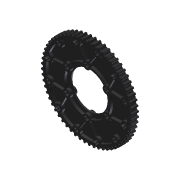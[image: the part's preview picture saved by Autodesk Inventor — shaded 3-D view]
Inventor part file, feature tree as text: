
AUTODESK INVENTOR PART (.ipt)
format: ipt  version: 2013 (Build 170138000, 138)  size: 1,892,352 bytes
history: native  units: in
note: dims shown in document units (in); Inventor stores cm internally (conversion verified against a paired STEP export)
features: fillet x1, other x1, move_body x1, imported_body x1
ambient origin geometry x8: Origin, YZ Plane, XZ Plane, XY Plane, X Axis, Y Axis, Z Axis, Center Point
feature tree (4):
  fillet  "Fillet3"  Radius=0.0753in
  other  "217-3200-002 Rev31"
  move_body  "Move Body1"
  imported_body  "Base1"
